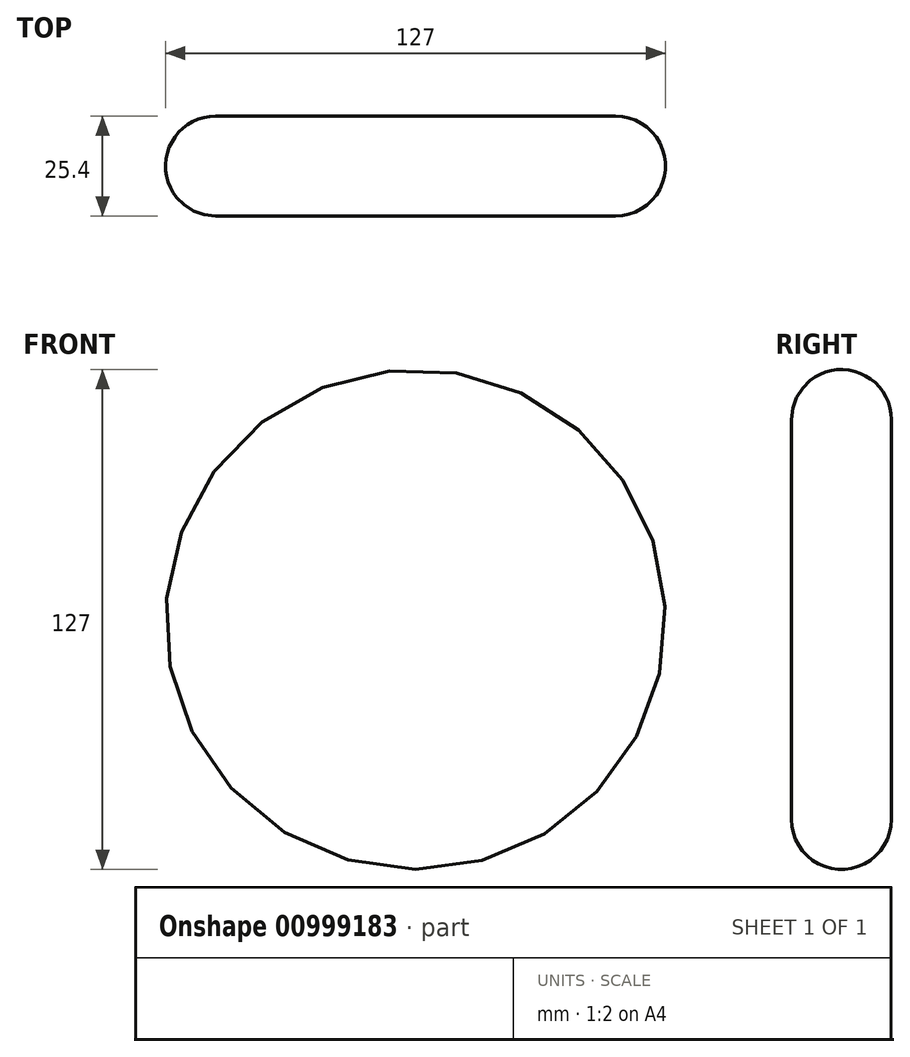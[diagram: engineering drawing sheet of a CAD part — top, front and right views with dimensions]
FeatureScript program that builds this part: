
annotation { "Feature Type Name" : "Feature", "Feature Type Description" : "" }
export const myFeature = defineFeature(function(context is Context, id is Id, definition is map)
    precondition{}
    {
        {
            var Q0;
            Q0=qCreatedBy(makeId("Right.planeOp"),FACE);
            var sketch = newSketch(context, id + "F0", { "sketchPlane" : qUnion([Q0])});
            skLineSegment(sketch, "E0", {"start": v(-139.36, 0) * mm, "end": v(141.77, 0) * mm, "construction": true});
            skLineSegment(sketch, "E1", {"start": v(-12.7, 0) * mm, "end": v(-12.7, 50.8) * mm});
            skLineSegment(sketch, "E2", {"start": v(12.7, 0) * mm, "end": v(12.7, 50.8) * mm});
            skArc(sketch, "E3", {"start": v(-12.7, 50.8) * mm, "mid": v(0, 63.5) * mm, "end": v(12.7, 50.8) * mm});
            skLineSegment(sketch, "E4", {"start": v(-12.7, 0) * mm, "end": v(12.7, 0) * mm});
            skSolve(sketch);
        }
        {
            var Q0;
            Q0 = qSketchRegion(id + "F0", true);
            var Q1;
            Q1=sQuery(id+"F0.wireOp",EDGE,"E0");
            revolve(context, id + "F1", {"surfaceOperationType" : NewSurfaceOperationType.NEW, "entities" : qUnion([Q0]), "axis" : qUnion([Q1]), "revolveType" : RevolveType.FULL});
        }
    });
